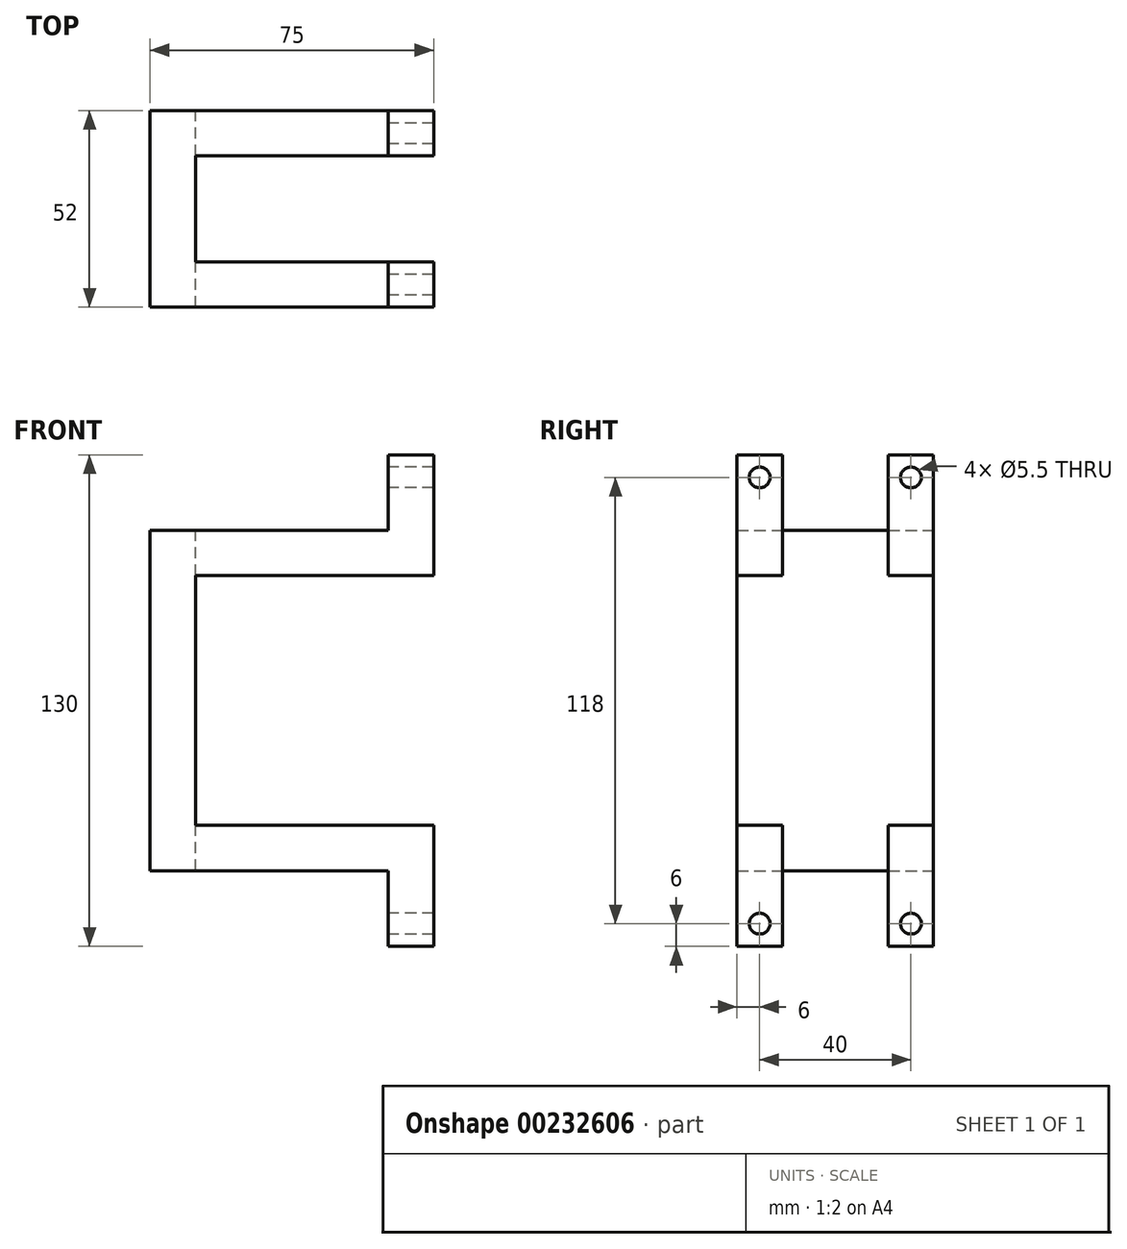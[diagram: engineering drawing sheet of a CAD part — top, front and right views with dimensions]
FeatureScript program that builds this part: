
annotation { "Feature Type Name" : "Feature", "Feature Type Description" : "" }
export const myFeature = defineFeature(function(context is Context, id is Id, definition is map)
    precondition{}
    {
        {
            var Q0;
            Q0=qCreatedBy(makeId("Front.planeOp"),FACE);
            var sketch = newSketch(context, id + "F0", { "sketchPlane" : qUnion([Q0])});
            skLineSegment(sketch, "E0.bottom", {"start": v(0, 0) * mm, "end": v(63, 0) * mm});
            skLineSegment(sketch, "E0.top", {"start": v(0, 90) * mm, "end": v(63, 90) * mm});
            skLineSegment(sketch, "E0.left", {"start": v(0, 0) * mm, "end": v(0, 12) * mm});
            skLineSegment(sketch, "E0.right", {"start": v(75, 0) * mm, "end": v(75, 12) * mm});
            skLineSegment(sketch, "E1", {"start": v(12, 78) * mm, "end": v(75, 78) * mm});
            skLineSegment(sketch, "E2", {"start": v(75, 12) * mm, "end": v(12, 12) * mm});
            skLineSegment(sketch, "E3.trimOffspring", {"start": v(0, 12) * mm, "end": v(0, 90) * mm});
            skLineSegment(sketch, "E4", {"start": v(12, 78) * mm, "end": v(12, 12) * mm});
            skLineSegment(sketch, "E5.trimOffspring", {"start": v(75, 78) * mm, "end": v(75, 90) * mm});
            skLineSegment(sketch, "E6.top", {"start": v(75, 110) * mm, "end": v(63, 110) * mm});
            skLineSegment(sketch, "E6.left", {"start": v(75, 90) * mm, "end": v(75, 110) * mm});
            skLineSegment(sketch, "E6.right", {"start": v(63, 90) * mm, "end": v(63, 110) * mm});
            skLineSegment(sketch, "E7.top", {"start": v(75, -20) * mm, "end": v(63, -20) * mm});
            skLineSegment(sketch, "E7.left", {"start": v(75, 0) * mm, "end": v(75, -20) * mm});
            skLineSegment(sketch, "E7.right", {"start": v(63, 0) * mm, "end": v(63, -20) * mm});
            skSolve(sketch);
        }
        {
            var Q0;
            Q0 = qSketchRegion(id + "F0", true);
            extrude(context, id + "F1", {"entities" : qUnion([Q0]), "depth" : 52 * mm});
        }
        {
            var Q0;
            Q0=makeQuery(id+"F1.opExtrude","SWEPT_FACE",FACE,{"disambiguationData":[OSD([sQuery(id+"F0.wireOp",EDGE,"E0.top")])]});
            var sketch = newSketch(context, id + "F2", { "sketchPlane" : qUnion([Q0])});
            skLineSegment(sketch, "E8.bottom", {"start": v(75, -12) * mm, "end": v(12, -12) * mm});
            skLineSegment(sketch, "E8.top", {"start": v(75, -40) * mm, "end": v(12, -40) * mm});
            skLineSegment(sketch, "E8.left", {"start": v(75, -12) * mm, "end": v(75, -40) * mm});
            skLineSegment(sketch, "E8.right", {"start": v(12, -12) * mm, "end": v(12, -40) * mm});
            skSolve(sketch);
        }
        {
            var Q0;
            Q0 = qSketchRegion(id + "F2", true);
            extrude(context, id + "F3", {"entities" : qUnion([Q0]), "operationType" : NewBodyOperationType.REMOVE, "endBound" : BoundingType.THROUGH_ALL, "oppositeDirection" : true, "depth" : 25 * mm, "hasSecondDirection" : true, "secondDirectionBound" : SecondDirectionBoundingType.THROUGH_ALL, "secondDirectionOppositeDirection" : false, "secondDirectionDepth" : 25 * mm});
        }
        {
            var Q0;
            {var subQ0=sQuery(id+"F0.wireOp",EDGE,"E6.right");Q0=makeQuery(id+"F3.boolean.opBoolean","SPLIT",FACE,{"disambiguationData":[TD([makeQuery(id+"F3.opExtrude","SWEPT_FACE",FACE,{"disambiguationData":[OSD([sQuery(id+"F2.wireOp",EDGE,"E8.bottom")])]})])],"derivedFrom":makeQuery(id+"F1.opExtrude","SWEPT_FACE",FACE,{"disambiguationData":[OSD([subQ0])]})});}
            var sketch = newSketch(context, id + "F4", { "sketchPlane" : qUnion([Q0])});
            skCircle(sketch, "E9", {"center": v(6, 104) * mm, "radius": 2.75 * mm});
            skCircle(sketch, "E10", {"center": v(46, 104) * mm, "radius": 2.75 * mm});
            skCircle(sketch, "E11", {"center": v(6, -14) * mm, "radius": 2.75 * mm});
            skCircle(sketch, "E12", {"center": v(46, -14) * mm, "radius": 2.75 * mm});
            skSolve(sketch);
        }
        {
            var Q0;
            Q0 = qSketchRegion(id + "F4", true);
            extrude(context, id + "F5", {"entities" : qUnion([Q0]), "operationType" : NewBodyOperationType.REMOVE, "endBound" : BoundingType.THROUGH_ALL, "oppositeDirection" : true, "depth" : 25 * mm});
        }
    });
